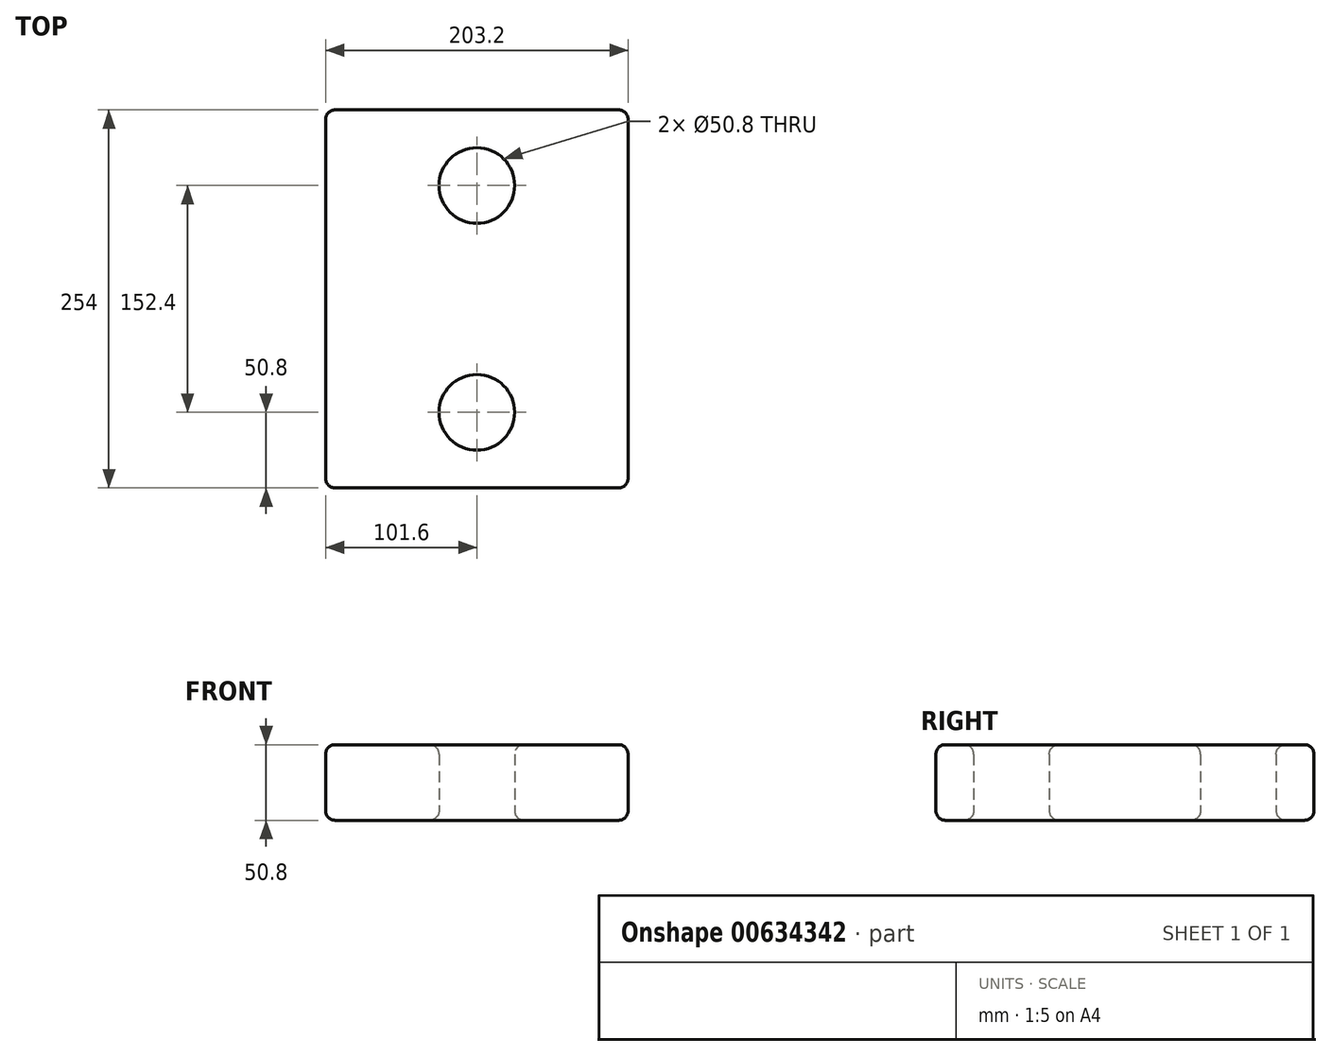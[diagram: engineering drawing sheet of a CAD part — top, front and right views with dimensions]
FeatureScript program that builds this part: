
annotation { "Feature Type Name" : "Feature", "Feature Type Description" : "" }
export const myFeature = defineFeature(function(context is Context, id is Id, definition is map)
    precondition{}
    {
        {
            var Q0;
            Q0=qCreatedBy(makeId("Top.planeOp"),FACE);
            var sketch = newSketch(context, id + "F0", { "sketchPlane" : qUnion([Q0])});
            skLineSegment(sketch, "E0.bottom", {"start": v(0, 0) * mm, "end": v(203.2, 0) * mm});
            skLineSegment(sketch, "E0.top", {"start": v(0, 254) * mm, "end": v(203.2, 254) * mm});
            skLineSegment(sketch, "E0.left", {"start": v(0, 0) * mm, "end": v(0, 254) * mm});
            skLineSegment(sketch, "E0.right", {"start": v(203.2, 0) * mm, "end": v(203.2, 254) * mm});
            skCircle(sketch, "E1", {"center": v(101.6, 203.2) * mm, "radius": 25.4 * mm});
            skPoint(sketch, "E1.centerSnap0", {"position": v(101.6, 0) * mm});
            skLineSegment(sketch, "E2", {"start": v(0, 127) * mm, "end": v(203.2, 127) * mm, "construction": true});
            skCircle(sketch, "E3.MirrorC", {"center": v(101.6, 50.8) * mm, "radius": 25.4 * mm});
            skSolve(sketch);
        }
        {
            var Q0;
            Q0=makeQuery(id+"F0.imprint","IMPRINT",FACE,{"disambiguationData":[TD([[makeQuery(id+"F0.imprint","IMPRINT",EDGE,{"derivedFrom":sQuery(id+"F0.wireOp",EDGE,"E0.bottom")}),1.0]])]});
            extrude(context, id + "F1", {"entities" : qUnion([Q0]), "depth" : 50.8 * mm, "offsetDistance" : 25.4 * mm});
        }
        {
            var Q0;
            Q0=makeQuery(id+"F1.opExtrude","CAP_EDGE",EDGE,{"disambiguationData":[OSD([sQuery(id+"F0.wireOp",EDGE,"E0.left")])],"isStart":false});
            var Q1;
            Q1=makeQuery(id+"F1.opExtrude","SWEPT_EDGE",EDGE,{"disambiguationData":[OSD([sQuery(id+"F0.wireOp",EDGE,"E0.top"),sQuery(id+"F0.wireOp",EDGE,"E0.left")])]});
            var Q2;
            Q2=makeQuery(id+"F1.opExtrude","CAP_EDGE",EDGE,{"disambiguationData":[OSD([sQuery(id+"F0.wireOp",EDGE,"E0.left")])],"isStart":true});
            var Q3;
            Q3=makeQuery(id+"F1.opExtrude","SWEPT_EDGE",EDGE,{"disambiguationData":[OSD([sQuery(id+"F0.wireOp",EDGE,"E0.bottom"),sQuery(id+"F0.wireOp",EDGE,"E0.left")])]});
            var Q4;
            Q4=makeQuery(id+"F1.opExtrude","CAP_EDGE",EDGE,{"disambiguationData":[OSD([sQuery(id+"F0.wireOp",EDGE,"E0.bottom")])],"isStart":false});
            var Q5;
            Q5=makeQuery(id+"F1.opExtrude","CAP_EDGE",EDGE,{"disambiguationData":[OSD([sQuery(id+"F0.wireOp",EDGE,"E0.bottom")])],"isStart":true});
            var Q6;
            Q6=makeQuery(id+"F1.opExtrude","SWEPT_EDGE",EDGE,{"disambiguationData":[OSD([sQuery(id+"F0.wireOp",EDGE,"E0.bottom"),sQuery(id+"F0.wireOp",EDGE,"E0.right")])]});
            var Q7;
            Q7=makeQuery(id+"F1.opExtrude","CAP_EDGE",EDGE,{"disambiguationData":[OSD([sQuery(id+"F0.wireOp",EDGE,"E3.MirrorC")])],"isStart":false});
            var Q8;
            Q8=makeQuery(id+"F1.opExtrude","CAP_EDGE",EDGE,{"disambiguationData":[OSD([sQuery(id+"F0.wireOp",EDGE,"E3.MirrorC")])],"isStart":true});
            var Q9;
            Q9=makeQuery(id+"F1.opExtrude","CAP_EDGE",EDGE,{"disambiguationData":[OSD([sQuery(id+"F0.wireOp",EDGE,"E1")])],"isStart":false});
            var Q10;
            Q10=makeQuery(id+"F1.opExtrude","CAP_EDGE",EDGE,{"disambiguationData":[OSD([sQuery(id+"F0.wireOp",EDGE,"E1")])],"isStart":true});
            var Q11;
            Q11=makeQuery(id+"F1.opExtrude","CAP_EDGE",EDGE,{"disambiguationData":[OSD([sQuery(id+"F0.wireOp",EDGE,"E0.top")])],"isStart":false});
            var Q12;
            Q12=makeQuery(id+"F1.opExtrude","CAP_EDGE",EDGE,{"disambiguationData":[OSD([sQuery(id+"F0.wireOp",EDGE,"E0.right")])],"isStart":false});
            var Q13;
            Q13=makeQuery(id+"F1.opExtrude","SWEPT_EDGE",EDGE,{"disambiguationData":[OSD([sQuery(id+"F0.wireOp",EDGE,"E0.top"),sQuery(id+"F0.wireOp",EDGE,"E0.right")])]});
            var Q14;
            Q14=makeQuery(id+"F1.opExtrude","CAP_EDGE",EDGE,{"disambiguationData":[OSD([sQuery(id+"F0.wireOp",EDGE,"E0.top")])],"isStart":true});
            var Q15;
            Q15=makeQuery(id+"F1.opExtrude","CAP_EDGE",EDGE,{"disambiguationData":[OSD([sQuery(id+"F0.wireOp",EDGE,"E0.right")])],"isStart":true});
            fillet(context, id + "F2", {"entities" : qUnion([Q0, Q1, Q2, Q3, Q4, Q5, Q6, Q7, Q8, Q9, Q10, Q11, Q12, Q13, Q14, Q15]), "radius" : 6.35 * mm, "tangentPropagation" : true, "allowEdgeOverflow" : false});
        }
    });
